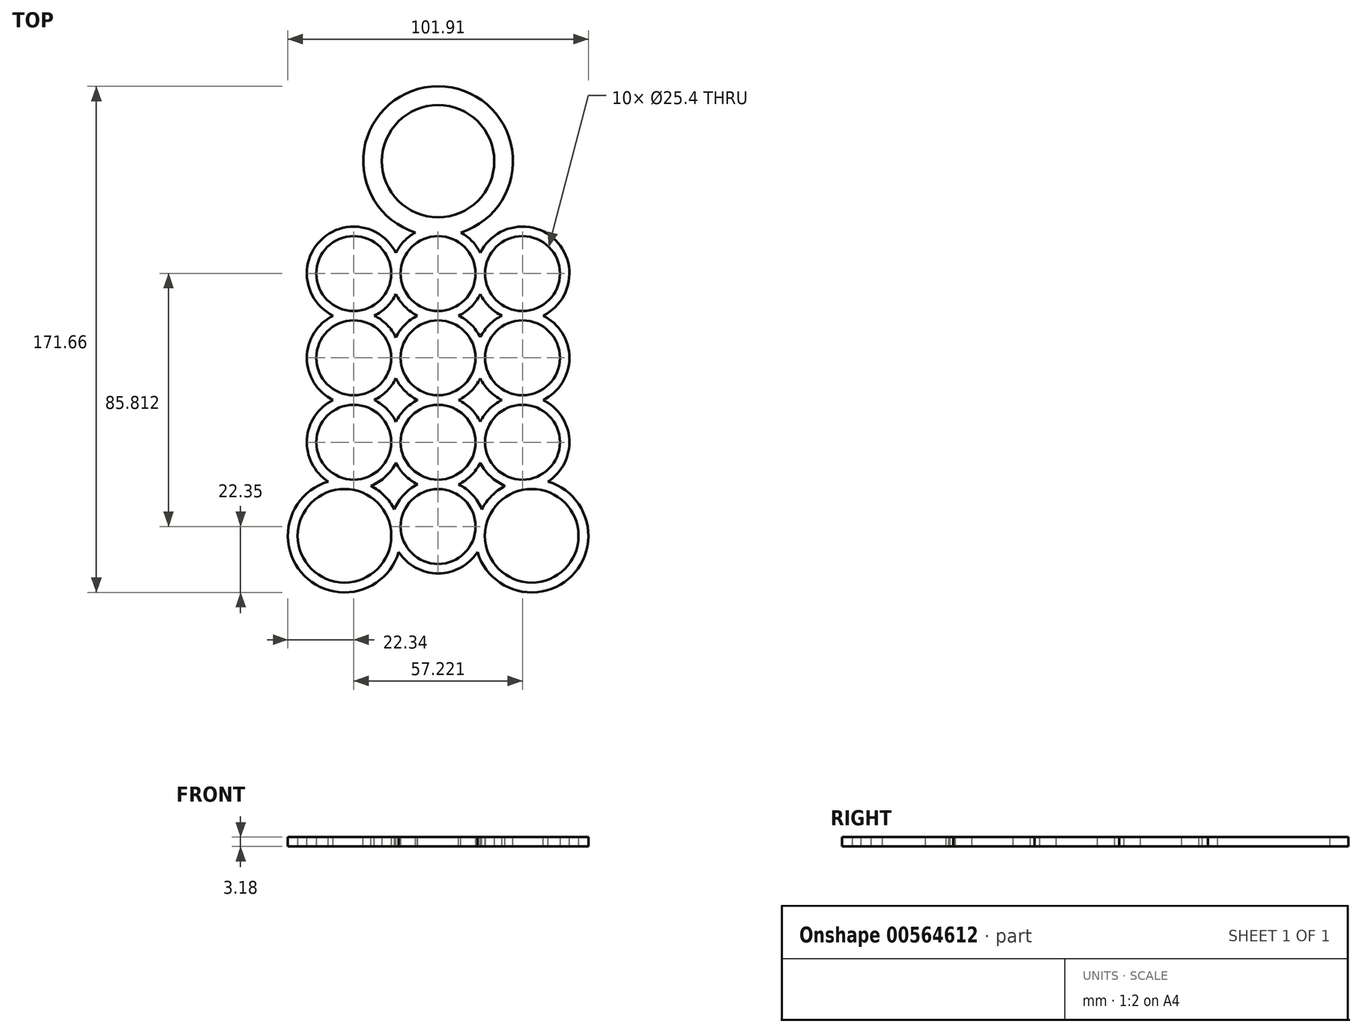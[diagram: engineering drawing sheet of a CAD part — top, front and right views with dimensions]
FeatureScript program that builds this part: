
annotation { "Feature Type Name" : "Feature", "Feature Type Description" : "" }
export const myFeature = defineFeature(function(context is Context, id is Id, definition is map)
    precondition{}
    {
        {
            var Q0;
            Q0=qCreatedBy(makeId("Top.planeOp"),FACE);
            var sketch = newSketch(context, id + "F0", { "sketchPlane" : qUnion([Q0])});
            skCircle(sketch, "E0", {"center": v(0, 0) * mm, "radius": 12.7 * mm});
            skCircle(sketch, "E1.0.1.0", {"center": v(0, 28.61) * mm, "radius": 12.7 * mm});
            skCircle(sketch, "E1.1.0.0", {"center": v(28.61, 0) * mm, "radius": 12.7 * mm});
            skCircle(sketch, "E1.1.1.0", {"center": v(28.61, 28.61) * mm, "radius": 12.7 * mm});
            skCircle(sketch, "E1.2.0.0", {"center": v(57.22, 0) * mm, "radius": 12.7 * mm});
            skCircle(sketch, "E1.2.1.0", {"center": v(57.22, 28.61) * mm, "radius": 12.7 * mm});
            skLineSegment(sketch, "E1.direction1", {"start": v(0, 0) * mm, "end": v(28.61, 0) * mm, "construction": true});
            skLineSegment(sketch, "E1.direction2", {"start": v(0, 0) * mm, "end": v(0, 28.61) * mm, "construction": true});
            skCircle(sketch, "E2", {"center": v(0, 57.21) * mm, "radius": 12.7 * mm});
            skCircle(sketch, "E3", {"center": v(28.61, 57.21) * mm, "radius": 12.7 * mm});
            skCircle(sketch, "E4", {"center": v(57.22, 57.21) * mm, "radius": 12.7 * mm});
            skCircle(sketch, "E5", {"center": v(28.61, -28.6) * mm, "radius": 12.7 * mm});
            skCircle(sketch, "E6", {"center": v(60.36, -31.75) * mm, "radius": 15.88 * mm});
            skCircle(sketch, "E7", {"center": v(-3.14, -31.75) * mm, "radius": 15.88 * mm});
            skCircle(sketch, "E8", {"center": v(28.61, 95.31) * mm, "radius": 19.05 * mm});
            skLineSegment(sketch, "E9.bottom", {"start": v(84.83, -65.82) * mm, "end": v(-27.6, -65.82) * mm});
            skLineSegment(sketch, "E9.top", {"start": v(84.83, 123.04) * mm, "end": v(-27.6, 123.04) * mm});
            skLineSegment(sketch, "E9.left", {"start": v(84.83, -65.82) * mm, "end": v(84.83, 123.04) * mm});
            skLineSegment(sketch, "E9.right", {"start": v(-27.6, -65.82) * mm, "end": v(-27.6, 123.04) * mm});
            skSolve(sketch);
        }
        {
            var Q0;
            Q0=makeQuery(id+"F0.imprint","IMPRINT",FACE,{"disambiguationData":[TD([[makeQuery(id+"F0.imprint","IMPRINT",EDGE,{"derivedFrom":sQuery(id+"F0.wireOp",EDGE,"E0")}),-1.0]])]});
            extrude(context, id + "F1", {"entities" : qUnion([Q0]), "depth" : 3.17 * mm, "offsetDistance" : 25.4 * mm});
        }
        {
            var Q0;
            Q0=makeQuery(id+"F1.opExtrude","CAP_FACE",FACE,{"disambiguationData":[OSD([sQuery(id+"F0.wireOp",EDGE,"E0"),sQuery(id+"F0.wireOp",EDGE,"E1.0.1.0"),sQuery(id+"F0.wireOp",EDGE,"E1.1.0.0"),sQuery(id+"F0.wireOp",EDGE,"E1.1.1.0"),sQuery(id+"F0.wireOp",EDGE,"E1.2.0.0"),sQuery(id+"F0.wireOp",EDGE,"E1.2.1.0"),sQuery(id+"F0.wireOp",EDGE,"E2"),sQuery(id+"F0.wireOp",EDGE,"E3"),sQuery(id+"F0.wireOp",EDGE,"E4"),sQuery(id+"F0.wireOp",EDGE,"E5"),sQuery(id+"F0.wireOp",EDGE,"E6"),sQuery(id+"F0.wireOp",EDGE,"E7"),sQuery(id+"F0.wireOp",EDGE,"E8"),sQuery(id+"F0.wireOp",EDGE,"E9.bottom"),sQuery(id+"F0.wireOp",EDGE,"E9.top"),sQuery(id+"F0.wireOp",EDGE,"E9.left"),sQuery(id+"F0.wireOp",EDGE,"E9.right")])],"isStart":false});
            var sketch = newSketch(context, id + "F2", { "sketchPlane" : qUnion([Q0])});
            skCircle(sketch, "E10", {"center": v(28.61, 95.31) * mm, "radius": 25.4 * mm});
            skCircle(sketch, "E11", {"center": v(28.61, 57.21) * mm, "radius": 15.91 * mm});
            skCircle(sketch, "E12", {"center": v(57.22, 57.21) * mm, "radius": 15.91 * mm});
            skCircle(sketch, "E13", {"center": v(0, 57.21) * mm, "radius": 15.91 * mm});
            skCircle(sketch, "E14", {"center": v(0, 28.61) * mm, "radius": 15.9 * mm});
            skCircle(sketch, "E15", {"center": v(28.61, 28.61) * mm, "radius": 15.91 * mm});
            skCircle(sketch, "E16", {"center": v(57.22, 28.61) * mm, "radius": 15.91 * mm});
            skCircle(sketch, "E17", {"center": v(57.22, 0) * mm, "radius": 15.91 * mm});
            skCircle(sketch, "E18", {"center": v(28.61, 0) * mm, "radius": 15.91 * mm});
            skCircle(sketch, "E19", {"center": v(0, 0) * mm, "radius": 15.91 * mm});
            skCircle(sketch, "E20", {"center": v(-3.14, -31.75) * mm, "radius": 19.2 * mm});
            skCircle(sketch, "E21", {"center": v(28.61, -28.6) * mm, "radius": 15.9 * mm});
            skCircle(sketch, "E22", {"center": v(60.36, -31.75) * mm, "radius": 19.2 * mm});
            skSolve(sketch);
        }
        {
            var Q0;
            {var subQ0=sQuery(id+"F2.wireOp",EDGE,"E19");var subQ1=sQuery(id+"F2.wireOp",EDGE,"E18");var subQ2=makeQuery(id+"F2.imprint","INTERSECT",VERTEX,{"disambiguationData":[OD(1.0)],"derivedFrom":[subQ1,subQ0]});Q0=makeQuery(id+"F2.imprint","IMPRINT",FACE,{"disambiguationData":[TD([[makeQuery(id+"F2.imprint","IMPRINT",EDGE,{"disambiguationData":[TD([[subQ2,-1.0]])],"derivedFrom":subQ1}),-1.0]])]});}
            var Q1;
            {var subQ0=sQuery(id+"F2.wireOp",EDGE,"E19");var subQ1=sQuery(id+"F2.wireOp",EDGE,"E14");var subQ2=makeQuery(id+"F2.imprint","INTERSECT",VERTEX,{"disambiguationData":[OD(1.0)],"derivedFrom":[subQ1,subQ0]});Q1=makeQuery(id+"F2.imprint","IMPRINT",FACE,{"disambiguationData":[TD([[makeQuery(id+"F2.imprint","IMPRINT",EDGE,{"disambiguationData":[TD([[subQ2,-1.0]])],"derivedFrom":subQ1}),-1.0]])]});}
            var Q2;
            {var subQ0=sQuery(id+"F2.wireOp",EDGE,"E13");var subQ1=sQuery(id+"F2.wireOp",EDGE,"E11");var subQ2=makeQuery(id+"F2.imprint","INTERSECT",VERTEX,{"disambiguationData":[OD(1.0)],"derivedFrom":[subQ1,subQ0]});Q2=makeQuery(id+"F2.imprint","IMPRINT",FACE,{"disambiguationData":[TD([[makeQuery(id+"F2.imprint","IMPRINT",EDGE,{"disambiguationData":[TD([[subQ2,-1.0]])],"derivedFrom":subQ1}),-1.0]])]});}
            var Q3;
            {var subQ0=sQuery(id+"F2.wireOp",EDGE,"E18");var subQ1=sQuery(id+"F2.wireOp",EDGE,"E15");var subQ2=makeQuery(id+"F2.imprint","INTERSECT",VERTEX,{"disambiguationData":[OD(1.0)],"derivedFrom":[subQ1,subQ0]});Q3=makeQuery(id+"F2.imprint","IMPRINT",FACE,{"disambiguationData":[TD([[makeQuery(id+"F2.imprint","IMPRINT",EDGE,{"disambiguationData":[TD([[subQ2,-1.0]])],"derivedFrom":subQ1}),-1.0]])]});}
            var Q4;
            {var subQ0=sQuery(id+"F2.wireOp",EDGE,"E18");var subQ1=sQuery(id+"F2.wireOp",EDGE,"E17");var subQ2=makeQuery(id+"F2.imprint","INTERSECT",VERTEX,{"disambiguationData":[OD(1.0)],"derivedFrom":[subQ1,subQ0]});Q4=makeQuery(id+"F2.imprint","IMPRINT",FACE,{"disambiguationData":[TD([[makeQuery(id+"F2.imprint","IMPRINT",EDGE,{"disambiguationData":[TD([[subQ2,-1.0]])],"derivedFrom":subQ1}),-1.0]])]});}
            var Q5;
            {var subQ0=sQuery(id+"F2.wireOp",EDGE,"E15");var subQ1=sQuery(id+"F2.wireOp",EDGE,"E11");var subQ2=makeQuery(id+"F2.imprint","INTERSECT",VERTEX,{"disambiguationData":[OD(1.0)],"derivedFrom":[subQ1,subQ0]});Q5=makeQuery(id+"F2.imprint","IMPRINT",FACE,{"disambiguationData":[TD([[makeQuery(id+"F2.imprint","IMPRINT",EDGE,{"disambiguationData":[TD([[subQ2,-1.0]])],"derivedFrom":subQ1}),-1.0]])]});}
            var Q6;
            Q6=makeQuery(id+"F2.imprint","IMPRINT",FACE,{"disambiguationData":[TD([[makeQuery(id+"F2.imprint","IMPRINT",EDGE,{"derivedFrom":makeQuery(id+"F1.opExtrude","CAP_EDGE",EDGE,{"disambiguationData":[OSD([sQuery(id+"F0.wireOp",EDGE,"E9.bottom")])],"isStart":false})}),-1.0]])]});
            extrude(context, id + "F3", {"entities" : qUnion([Q0, Q1, Q2, Q3, Q4, Q5, Q6]), "operationType" : NewBodyOperationType.REMOVE, "oppositeDirection" : true, "depth" : 25.4 * mm, "offsetDistance" : 25.4 * mm});
        }
    });
